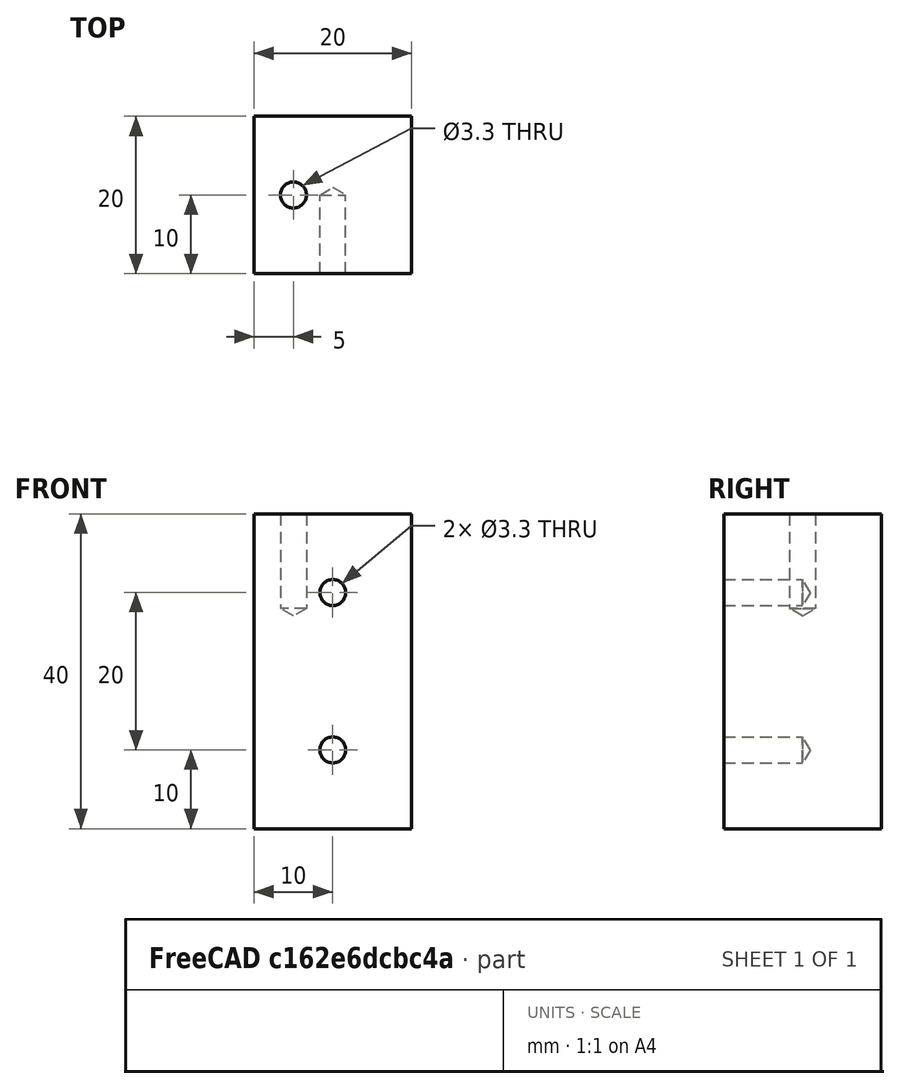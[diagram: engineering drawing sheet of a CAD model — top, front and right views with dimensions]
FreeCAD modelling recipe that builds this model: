
FCSTD DOCUMENT  (FreeCAD 1.0R39319 (Git))
Label: OCT-URBLK-AB
License: Creative Commons Attribution 4.0
LicenseURL: https://creativecommons.org/licenses/by/4.0/
objects: TechDraw::DrawViewDimension×9, Sketcher::SketchObject×3, PartDesign::Hole×2, TechDraw::DrawProjGroupItem×2, PartDesign::Pad×1, PartDesign::Body×1, TechDraw::DrawSVGTemplate×1, TechDraw::DrawProjGroup×1, TechDraw::DrawPage×1
note: 29 computed .brp shape members not serialized (recipe doc carries the construction recipe); baked Part::Feature solids carry a one-line shape summary decoded from their .brp

FEATURE [Sketcher::SketchObject] Sketch
  ArcFitTolerance = 1e-06
  AttachmentSupport = -> [XY_Plane]
  FullyConstrained = true
  MakeInternals = false
  MapMode = 5
  sketch-geometry (4):
    g0: LineSegment StartX=65 StartY=0 StartZ=0 EndX=85 EndY=0 EndZ=0
    g1: LineSegment StartX=85 StartY=0 StartZ=0 EndX=85 EndY=20 EndZ=0
    g2: LineSegment StartX=65 StartY=20 StartZ=0 EndX=65 EndY=0 EndZ=0
    g3: LineSegment StartX=65 StartY=20 StartZ=0 EndX=85 EndY=20 EndZ=0
  constraints (12):
    c: PointOnObject(g0,g-1)
    c: PointOnObject(g0,g-1)
    c: Coincident(g0,g1)
    c: Vertical(g1)
    c: Vertical(g2)
    c: DistanceX(g0,g0) = 20
    c: DistanceX(g-1,g0) = 85
    c: Coincident(g2,g0)
    c: DistanceY(g2,g2) = 20
    c: Coincident(g2,g3)
    c: Horizontal(g3)
    c: Coincident(g3,g1)
FEATURE [PartDesign::Pad] Pad
  Direction = (0,0,1)
  Length = 40
  Length2 = 10
  Profile = -> Sketch
  ReferenceAxis = -> Sketch [N_Axis]
  Suppressed = false
  Type = 0
FEATURE [Sketcher::SketchObject] Sketch001
  ArcFitTolerance = 1e-06
  AttachmentSupport = -> [Pad]
  FullyConstrained = true
  MakeInternals = false
  MapMode = 5
  Placement = pos=(0,0,0) rot=(1,0,0;1.5708rad)
  sketch-geometry (3):
    g0: Circle CenterX=75 CenterY=30 CenterZ=0 NormalX=0 NormalY=0 NormalZ=1 AngleXU=0 Radius=2
    g1: Circle CenterX=75 CenterY=10 CenterZ=0 NormalX=0 NormalY=0 NormalZ=1 AngleXU=0 Radius=2
    g2: LineSegment [constr] StartX=75 StartY=30 StartZ=0 EndX=75 EndY=10 EndZ=0
  constraints (8):
    c: Coincident(g2,g0)
    c: Coincident(g2,g1)
    c: Vertical(g2)
    c: Equal(g0,g1)
    c: Diameter(g0) = 4
    c: DistanceX(g-1,g1) = 75
    c: Distance(g1,g-1) = 10
    c: DistanceY(g2,g2) = 20
FEATURE [PartDesign::Hole] Hole
  BaseFeature = -> Pad
  CustomThreadClearance = 0
  Depth = 10
  DepthType = 0
  Diameter = 3.3
  DrillForDepth = false
  DrillPoint = 1
  DrillPointAngle = 118
  HoleCutCountersinkAngle = 90
  HoleCutCustomValues = false
  HoleCutDepth = 0
  HoleCutDiameter = 6.1
  HoleCutType = 0
  ModelThread = false
  Profile = -> Sketch001
  Suppressed = false
  Tapered = false
  TaperedAngle = 90
  ThreadClass = 0
  ThreadDepth = 10
  ThreadDepthType = 0
  ThreadDirection = 0
  ThreadFit = 0
  ThreadSize = 11
  ThreadType = 1
  Threaded = true
  UseCustomThreadClearance = false
FEATURE [Sketcher::SketchObject] Sketch002
  ArcFitTolerance = 1e-06
  AttachmentSupport = -> [Hole]
  FullyConstrained = true
  MakeInternals = false
  MapMode = 5
  Placement = pos=(0,0,40) rot=(0,0,1;0rad)
  sketch-geometry (1):
    g0: Circle CenterX=70 CenterY=10 CenterZ=0 NormalX=0 NormalY=0 NormalZ=1 AngleXU=0 Radius=2
  constraints (3):
    c: Diameter(g0) = 4
    c: Distance(g0,g-2) = 70
    c: Distance(g0,g-1) = 10
FEATURE [PartDesign::Hole] Hole001
  BaseFeature = -> Hole
  CustomThreadClearance = 0
  Depth = 12
  DepthType = 0
  Diameter = 3.3
  DrillForDepth = false
  DrillPoint = 1
  DrillPointAngle = 118
  HoleCutCountersinkAngle = 90
  HoleCutCustomValues = false
  HoleCutDepth = 0
  HoleCutDiameter = 6.1
  HoleCutType = 0
  ModelThread = false
  Profile = -> Sketch002
  Suppressed = false
  Tapered = false
  TaperedAngle = 90
  ThreadClass = 0
  ThreadDepth = 12
  ThreadDepthType = 0
  ThreadDirection = 0
  ThreadFit = 0
  ThreadSize = 11
  ThreadType = 1
  Threaded = true
  UseCustomThreadClearance = false
FEATURE [PartDesign::Body] Body  label="OCT-URBLK-AB"
  AllowCompound = false
  Group = -> [Sketch,Pad,Sketch001,Hole,Sketch002,Hole001]
  Origin = -> Origin
  Tip = -> Hole001
FEATURE [TechDraw::DrawSVGTemplate] Template
  EditableTexts = approval_person=S. Aphelion; creator=Michael Stoll; date_of_issue=13/02/2026; document_status=In preparation; document_type=Component Drawing; drawing_number=DN; general_tolerances=ISO 2768-m; language_code=EN; part_material=Aluminium 6082 T6; responsible_department=RD; revision_index=A; scale=2 : 1; sheet_number=1 / 1; supplementary_title_1=Upper Right Panel Block; title=OCT-URBLK-AB
  Height = 297
  Orientation = 1
  Template = C:/Program Files/FreeCAD 1.0/data/Mod/TechDraw/Templates/A3_Landscape_ISO5457_advanced.svg
  Width = 420
FEATURE [TechDraw::DrawProjGroupItem] View  label="Front"
  CoarseView = false
  Direction = (0,-1,0)
  Focus = 100
  HardHidden = false
  IsoCount = 0
  IsoHidden = false
  IsoVisible = false
  LockPosition = true
  Perspective = false
  Rotation = 0
  RotationVector = (1,0,0)
  Scale = 2
  ScaleType = 2
  ScrubCount = 1
  SeamHidden = false
  SeamVisible = false
  SmoothHidden = false
  SmoothVisible = true
  Source = -> [Body]
  Type = 0
  X = 0
  XDirection = (1,0,0)
  Y = 0
FEATURE [TechDraw::DrawProjGroupItem] ProjItem  label="Top"
  CoarseView = false
  Direction = (0,0,1)
  Focus = 100
  HardHidden = false
  IsoCount = 0
  IsoHidden = false
  IsoVisible = false
  LockPosition = false
  Perspective = false
  Rotation = 0
  RotationVector = (1,0,0)
  Scale = 2
  ScaleType = 0
  ScrubCount = 1
  SeamHidden = false
  SeamVisible = false
  SmoothHidden = false
  SmoothVisible = true
  Source = -> [Body]
  Type = 4
  X = 0
  XDirection = (1,0,0)
  Y = 110
FEATURE [TechDraw::DrawProjGroup] ProjGroup
  Anchor = -> View
  AutoDistribute = true
  LockPosition = false
  ProjectionType = 1
  Rotation = 0
  Scale = 2
  ScaleType = 0
  Source = -> [Body]
  Views = -> [View,ProjItem]
  X = 158.246
  Y = 108.433
  spacingX = 15
  spacingY = 50
FEATURE [TechDraw::DrawViewDimension] Dimension
  AngleOverride = false
  Arbitrary = false
  ArbitraryTolerances = false
  BoxCorners = (2) [(-20,-40,0),(20,40,0)]
  EqualTolerance = true
  ExtensionAngle = 0
  FormatSpec = %.1f
  FormatSpecOverTolerance = %+.1f
  FormatSpecUnderTolerance = %+.1f
  Inverted = false
  LineAngle = 0
  LockPosition = false
  MeasureType = 1
  OverTolerance = 0
  References2D = -> [View]
  Rotation = 0
  Scale = 2
  ScaleType = 0
  TheoreticalExact = false
  Type = 2
  UnderTolerance = 0
  X = 32.4665
  Y = 0
FEATURE [TechDraw::DrawViewDimension] Dimension001
  AngleOverride = false
  Arbitrary = false
  ArbitraryTolerances = false
  BoxCorners = (2) [(-20,-40,0),(20,40,0)]
  EqualTolerance = true
  ExtensionAngle = 0
  FormatSpec = %.1f
  FormatSpecOverTolerance = %+.1f
  FormatSpecUnderTolerance = %+.1f
  Inverted = false
  LineAngle = 0
  LockPosition = false
  MeasureType = 1
  OverTolerance = 0
  References2D = -> [View]
  Rotation = 0
  Scale = 2
  ScaleType = 0
  TheoreticalExact = false
  Type = 1
  UnderTolerance = 0
  X = 0
  Y = -61.7063
FEATURE [TechDraw::DrawViewDimension] Dimension002
  AngleOverride = false
  Arbitrary = false
  ArbitraryTolerances = false
  BoxCorners = (2) [(-20,-40,0),(20,40,0)]
  EqualTolerance = true
  ExtensionAngle = 0
  FormatSpec = %.1f
  FormatSpecOverTolerance = %+.1f
  FormatSpecUnderTolerance = %+.1f
  Inverted = false
  LineAngle = 0
  LockPosition = false
  MeasureType = 1
  OverTolerance = 0
  References2D = -> [View]
  Rotation = 0
  Scale = 2
  ScaleType = 0
  TheoreticalExact = false
  Type = 0
  UnderTolerance = 0
  X = -39.5647
  Y = -30
FEATURE [TechDraw::DrawViewDimension] Dimension003
  AngleOverride = false
  Arbitrary = false
  ArbitraryTolerances = false
  BoxCorners = (2) [(-20,-40,0),(20,40,0)]
  EqualTolerance = true
  ExtensionAngle = 0
  FormatSpec = %.1f
  FormatSpecOverTolerance = %+.1f
  FormatSpecUnderTolerance = %+.1f
  Inverted = false
  LineAngle = 0
  LockPosition = false
  MeasureType = 1
  OverTolerance = 0
  References2D = -> [View]
  Rotation = 0
  Scale = 2
  ScaleType = 0
  TheoreticalExact = false
  Type = 2
  UnderTolerance = 0
  X = -39.5647
  Y = 0
FEATURE [TechDraw::DrawViewDimension] Dimension005
  AngleOverride = false
  Arbitrary = false
  ArbitraryTolerances = false
  BoxCorners = (2) [(-20,-20,0),(20,20,0)]
  EqualTolerance = true
  ExtensionAngle = 0
  FormatSpec = %.1f
  FormatSpecOverTolerance = %+.1f
  FormatSpecUnderTolerance = %+.1f
  Inverted = false
  LineAngle = 0
  LockPosition = false
  MeasureType = 1
  OverTolerance = 0
  References2D = -> [ProjItem]
  Rotation = 0
  Scale = 2
  ScaleType = 0
  TheoreticalExact = false
  Type = 2
  UnderTolerance = 0
  X = -60.5712
  Y = 0
FEATURE [TechDraw::DrawViewDimension] Dimension012
  AngleOverride = false
  Arbitrary = false
  ArbitraryTolerances = false
  BoxCorners = (2) [(-20,-40,0),(20,40,0)]
  EqualTolerance = true
  ExtensionAngle = 0
  FormatSpec = ⌀%.1f
  FormatSpecOverTolerance = %+.1f
  FormatSpecUnderTolerance = %+.1f
  Inverted = false
  LineAngle = 0
  LockPosition = false
  MeasureType = 1
  OverTolerance = 0
  References2D = -> [View]
  Rotation = 0
  Scale = 2
  ScaleType = 0
  TheoreticalExact = false
  Type = 5
  UnderTolerance = 0
  X = -39.8537
  Y = 56.1716
FEATURE [TechDraw::DrawViewDimension] Dimension013
  AngleOverride = false
  Arbitrary = false
  ArbitraryTolerances = false
  BoxCorners = (2) [(-20,-20,0),(20,20,0)]
  EqualTolerance = true
  ExtensionAngle = 0
  FormatSpec = %.1f
  FormatSpecOverTolerance = %+.1f
  FormatSpecUnderTolerance = %+.1f
  Inverted = false
  LineAngle = 0
  LockPosition = false
  MeasureType = 1
  OverTolerance = 0
  References2D = -> [ProjItem]
  Rotation = 0
  Scale = 2
  ScaleType = 0
  TheoreticalExact = false
  Type = 0
  UnderTolerance = 0
  X = 46.6104
  Y = 10
FEATURE [TechDraw::DrawViewDimension] Dimension014
  AngleOverride = false
  Arbitrary = false
  ArbitraryTolerances = false
  BoxCorners = (2) [(-20,-20,0),(20,20,0)]
  EqualTolerance = true
  ExtensionAngle = 0
  FormatSpec = ⌀%.1f
  FormatSpecOverTolerance = %+.1f
  FormatSpecUnderTolerance = %+.1f
  Inverted = false
  LineAngle = 0
  LockPosition = false
  MeasureType = 1
  OverTolerance = 0
  References2D = -> [ProjItem]
  Rotation = 0
  Scale = 2
  ScaleType = 0
  TheoreticalExact = false
  Type = 5
  UnderTolerance = 0
  X = 66.7841
  Y = -18.8481
FEATURE [TechDraw::DrawViewDimension] Dimension015
  AngleOverride = false
  Arbitrary = false
  ArbitraryTolerances = false
  BoxCorners = (2) [(-20,-20,0),(20,20,0)]
  EqualTolerance = true
  ExtensionAngle = 0
  FormatSpec = %.1f
  FormatSpecOverTolerance = %+.1f
  FormatSpecUnderTolerance = %+.1f
  Inverted = false
  LineAngle = 0
  LockPosition = false
  MeasureType = 1
  OverTolerance = 0
  References2D = -> [ProjItem]
  Rotation = 0
  Scale = 2
  ScaleType = 0
  TheoreticalExact = false
  Type = 0
  UnderTolerance = 0
  X = -15
  Y = 52.3505
FEATURE [TechDraw::DrawPage] Page
  KeepUpdated = true
  NextBalloonIndex = 1
  ProjectionType = 1
  Scale = 2
  Template = -> Template
  Views = -> [ProjGroup,Dimension,Dimension001,Dimension002,Dimension003,Dimension005,Dimension012,Dimension013,Dimension014,Dimension015]
